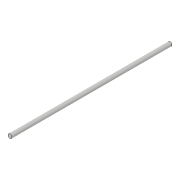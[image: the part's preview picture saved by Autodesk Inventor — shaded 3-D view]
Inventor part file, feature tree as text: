
AUTODESK INVENTOR PART (.ipt)
format: ipt  version: 2018.3 (Build 223284000, 284)  size: 69,632 bytes
history: native  units: in
note: dims shown in document units (in); Inventor stores cm internally (conversion verified against a paired STEP export)
features: extrude x1, sketch x1
ambient origin geometry x8: Origin, YZ Plane, XZ Plane, XY Plane, X Axis, Y Axis, Z Axis, Center Point
bodies: Solid1 (feature_tree)
feature tree (2):
  extrude  "Extrusion1"  Depth=5.0in TaperAngle=0.0deg
  sketch  "Sketch1"  dims[d0=0.125in d1=5.0in d2=0.0in]
